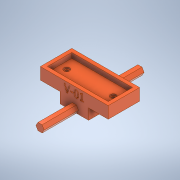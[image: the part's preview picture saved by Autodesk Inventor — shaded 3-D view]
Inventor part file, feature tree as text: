
AUTODESK INVENTOR PART (.ipt)
format: ipt  version: 2021.2 (Build 252289000, 289)  size: 226,816 bytes
history: native  units: in
note: dims shown in document units (in); Inventor stores cm internally (conversion verified against a paired STEP export)
features: sketch x5, extrude x5, hole x1, mirror x1
ambient origin geometry x8: Origin, YZ Plane, XZ Plane, XY Plane, X Axis, Y Axis, Z Axis, Center Point
bodies: Solid1 (feature_tree)
feature tree (12):
  sketch  "Sketch1"  dims[d0=1.7in d1=4.25in]
  extrude  "Extrusion1"  Depth=4.25in
  extrude  "Extrusion2"  Depth=0.25in
  hole  "Hole1"  [1 undecoded]
  extrude  "Extrusion6"  TaperAngle=0.0deg  [1 undecoded]
  extrude  "Extrusion8"  Depth=0.5in
  extrude  "Extrusion9"  Depth=0.375in
  mirror  "Mirror5"
  sketch  "Sketch2"  dims[d2=0.25in d3=0.25in]
  sketch  "Sketch5"  dims[d4=0.475in d5=0.0in]
  sketch  "Sketch11"  dims[d6=0.35in d7=0.0in]
  sketch  "Sketch12"  dims[d8=0.5in d9=0.5in d10=0.201in d11=0.75in d12=0.4in d13=0.1in d14=0.5635in d15=1.0in d16=0.8108in d17=0.375in d24=0.375in d27=2.0in d28=2.2in d29=0.75in d30=0.0in d84=0.1in d85=0.0in d86=0.5in d87=2.4in d88=0.0in]
note: 2 required parameter values undecoded (feature->parameter linkage not recoverable at this tier; creation-order binding heuristic only, values carry confidence <= 0.55)
